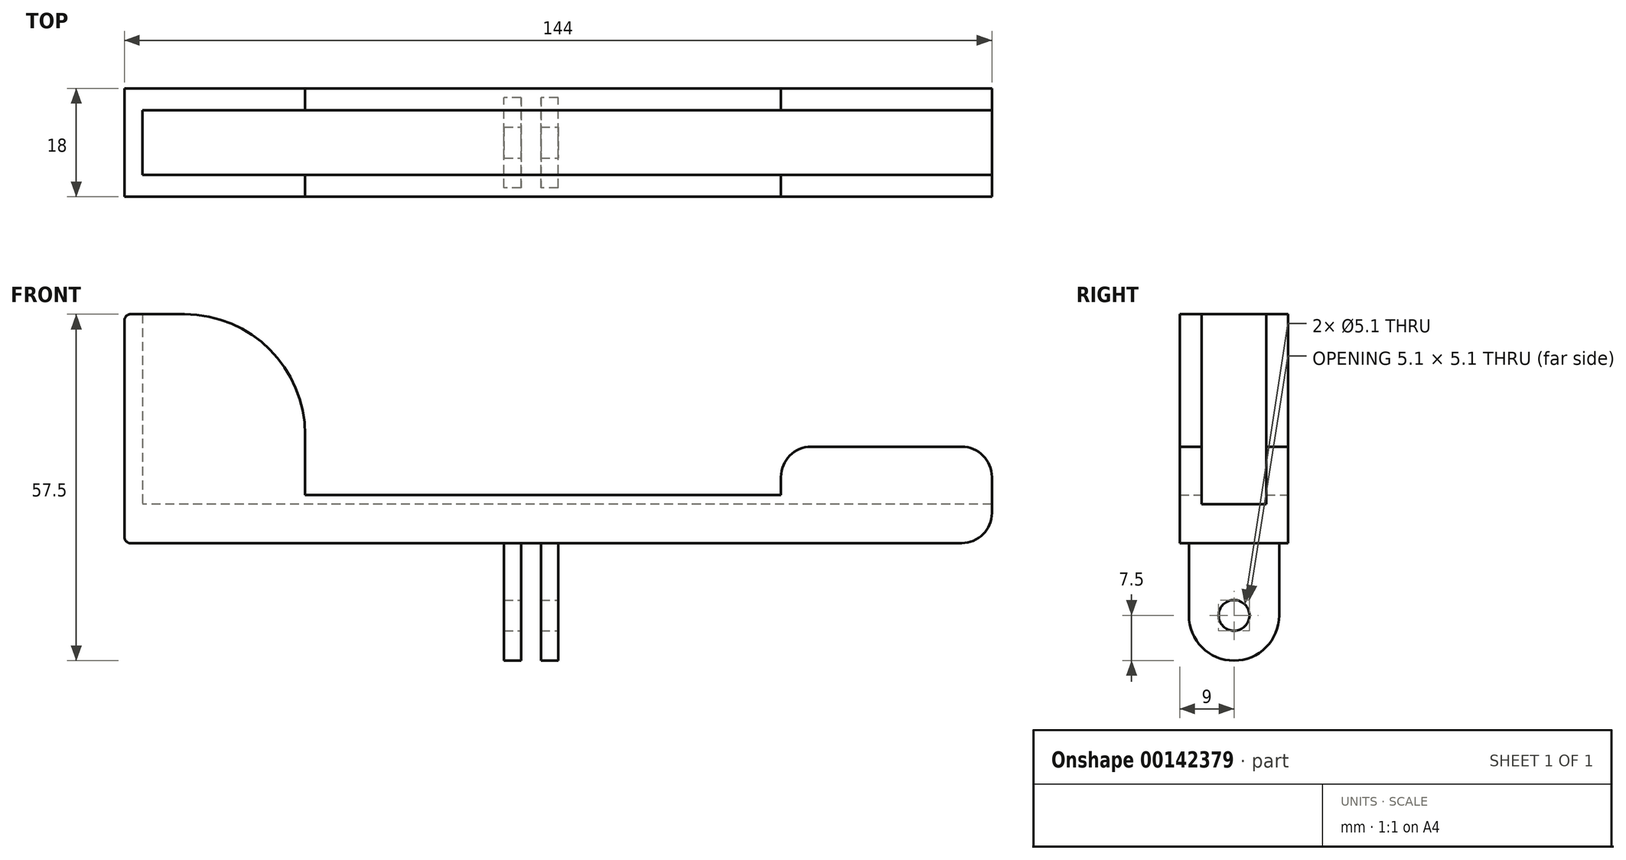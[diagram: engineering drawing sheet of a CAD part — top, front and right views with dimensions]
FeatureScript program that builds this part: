
annotation { "Feature Type Name" : "Feature", "Feature Type Description" : "" }
export const myFeature = defineFeature(function(context is Context, id is Id, definition is map)
    precondition{}
    {
        {
            var Q0;
            Q0=qCreatedBy(makeId("Right.planeOp"),FACE);
            var sketch = newSketch(context, id + "F0", { "sketchPlane" : qUnion([Q0])});
            skCircle(sketch, "E0", {"center": v(0, 0) * mm, "radius": 7.5 * mm});
            skSolve(sketch);
        }
        {
            var Q0;
            Q0=qCreatedBy(makeId("Right.planeOp"),FACE);
            var sketch = newSketch(context, id + "F1", { "sketchPlane" : qUnion([Q0])});
            skLineSegment(sketch, "E1.bottom", {"start": v(-7.5, 0) * mm, "end": v(7.5, 0) * mm});
            skLineSegment(sketch, "E1.top", {"start": v(-7.5, 12) * mm, "end": v(7.5, 12) * mm});
            skLineSegment(sketch, "E1.left", {"start": v(-7.5, 0) * mm, "end": v(-7.5, 12) * mm});
            skLineSegment(sketch, "E1.right", {"start": v(7.5, 0) * mm, "end": v(7.5, 12) * mm});
            skSolve(sketch);
        }
        {
            var Q0;
            Q0 = qSketchRegion(id + "F0", true);
            var Q1;
            Q1 = qSketchRegion(id + "F1", true);
            extrude(context, id + "F2", {"entities" : qUnion([Q0, Q1]), "flatOperationType" : FlatOperationType.REMOVE, "offsetDistance" : 25 * mm, "depth" : 9 * mm, "domain" : OperationDomain.MODEL, "symmetric" : true});
        }
        {
            var Q0;
            Q0=makeQuery(id+"F2.opExtrude","CAP_FACE",FACE,{"disambiguationData":[OSD([sQuery(id+"F1.wireOp",EDGE,"E1.bottom"),sQuery(id+"F1.wireOp",EDGE,"E1.top"),sQuery(id+"F1.wireOp",EDGE,"E1.left"),sQuery(id+"F1.wireOp",EDGE,"E1.right")])],"isStart":false});
            var sketch = newSketch(context, id + "F3", { "sketchPlane" : qUnion([Q0])});
            skLineSegment(sketch, "E2.bottom", {"start": v(-9, 12) * mm, "end": v(9, 12) * mm});
            skLineSegment(sketch, "E2.top", {"start": v(-9, 20) * mm, "end": v(9, 20) * mm});
            skLineSegment(sketch, "E2.left", {"start": v(-9, 12) * mm, "end": v(-9, 20) * mm});
            skLineSegment(sketch, "E2.right", {"start": v(9, 12) * mm, "end": v(9, 20) * mm});
            skSolve(sketch);
        }
        {
            var Q0;
            Q0 = qSketchRegion(id + "F3", true);
            extrude(context, id + "F4", {"entities" : qUnion([Q0]), "operationType" : NewBodyOperationType.ADD, "oppositeDirection" : true, "depth" : 144 * mm, "symmetric" : true});
        }
        {
            var Q0;
            Q0=qCreatedBy(makeId("Front.planeOp"),FACE);
            var sketch = newSketch(context, id + "F5", { "sketchPlane" : qUnion([Q0])});
            skLineSegment(sketch, "E3.bottom", {"start": v(-67.5, 20) * mm, "end": v(-37.5, 20) * mm});
            skLineSegment(sketch, "E3.top", {"start": v(-67.5, 50) * mm, "end": v(-37.5, 50) * mm});
            skLineSegment(sketch, "E3.left", {"start": v(-67.5, 20) * mm, "end": v(-67.5, 50) * mm});
            skLineSegment(sketch, "E3.right", {"start": v(-37.5, 20) * mm, "end": v(-37.5, 50) * mm});
            skSolve(sketch);
        }
        {
            var Q0;
            Q0=makeQuery(id+"F5.imprint","IMPRINT",FACE,{"disambiguationData":[TD([[makeQuery(id+"F5.imprint","IMPRINT",EDGE,{"derivedFrom":sQuery(id+"F5.wireOp",EDGE,"E3.bottom")}),1.0]])]});
            extrude(context, id + "F6", {"entities" : qUnion([Q0]), "oppositeDirection" : true, "depth" : 18 * mm, "offsetDistance" : 25 * mm, "symmetric" : true});
        }
        {
            var Q0;
            Q0=qCreatedBy(makeId("Front.planeOp"),FACE);
            var sketch = newSketch(context, id + "F7", { "sketchPlane" : qUnion([Q0])});
            skLineSegment(sketch, "E4.bottom", {"start": v(76.5, 20) * mm, "end": v(41.5, 20) * mm});
            skLineSegment(sketch, "E4.top", {"start": v(76.5, 28) * mm, "end": v(41.5, 28) * mm});
            skLineSegment(sketch, "E4.left", {"start": v(76.5, 20) * mm, "end": v(76.5, 28) * mm});
            skLineSegment(sketch, "E4.right", {"start": v(41.5, 20) * mm, "end": v(41.5, 28) * mm});
            skSolve(sketch);
        }
        {
            var Q0;
            Q0=makeQuery(id+"F7.imprint","IMPRINT",FACE,{"disambiguationData":[TD([[makeQuery(id+"F7.imprint","IMPRINT",EDGE,{"derivedFrom":sQuery(id+"F7.wireOp",EDGE,"E4.bottom")}),-1.0]])]});
            extrude(context, id + "F8", {"entities" : qUnion([Q0]), "depth" : 18 * mm, "offsetDistance" : 25 * mm, "symmetric" : true});
        }
        {
            var Q0;
            Q0=qCreatedBy(makeId("Front.planeOp"),FACE);
            var sketch = newSketch(context, id + "F9", { "sketchPlane" : qUnion([Q0])});
            skLineSegment(sketch, "E5.bottom", {"start": v(76.5, 53.5) * mm, "end": v(-64.5, 53.5) * mm});
            skLineSegment(sketch, "E5.top", {"start": v(76.5, 18.5) * mm, "end": v(-64.5, 18.5) * mm});
            skLineSegment(sketch, "E5.left", {"start": v(-64.5, 53.5) * mm, "end": v(-64.5, 18.5) * mm});
            skLineSegment(sketch, "E5.right", {"start": v(76.5, 53.5) * mm, "end": v(76.5, 18.5) * mm});
            skSolve(sketch);
        }
        {
            var Q0;
            Q0 = qSketchRegion(id + "F9", true);
            extrude(context, id + "F10", {"entities" : qUnion([Q0]), "depth" : 10.7 * mm, "flatOperationType" : FlatOperationType.REMOVE, "offsetDistance" : 25 * mm, "domain" : OperationDomain.MODEL, "symmetric" : true});
        }
        {
            var Q0;
            Q0=makeQuery(id+"F2.opExtrude","SWEPT_BODY",BODY,{"disambiguationData":[OSD([sQuery(id+"F0.wireOp",EDGE,"E0")])]});
            var Q1;
            Q1=makeQuery(id+"F2.opExtrude","SWEPT_BODY",BODY,{"disambiguationData":[OSD([sQuery(id+"F1.wireOp",EDGE,"E1.bottom"),sQuery(id+"F1.wireOp",EDGE,"E1.top"),sQuery(id+"F1.wireOp",EDGE,"E1.left"),sQuery(id+"F1.wireOp",EDGE,"E1.right")])]});
            var Q2;
            Q2=makeQuery(id+"F6.opExtrude","SWEPT_BODY",BODY,{"disambiguationData":[OSD([sQuery(id+"F5.wireOp",EDGE,"E3.bottom"),sQuery(id+"F5.wireOp",EDGE,"E3.top"),sQuery(id+"F5.wireOp",EDGE,"E3.left"),sQuery(id+"F5.wireOp",EDGE,"E3.right")])]});
            var Q3;
            Q3=makeQuery(id+"F8.opExtrude","SWEPT_BODY",BODY,{"disambiguationData":[OSD([sQuery(id+"F7.wireOp",EDGE,"E4.bottom"),sQuery(id+"F7.wireOp",EDGE,"E4.top"),sQuery(id+"F7.wireOp",EDGE,"E4.left"),sQuery(id+"F7.wireOp",EDGE,"E4.right")])]});
            booleanBodies(context, id + "F11", {"operationType" : BooleanOperationType.UNION, "tools" : qUnion([Q0, Q1, Q2, Q3])});
        }
        {
            var Q0;
            Q0=makeQuery(id+"F10.opExtrude","SWEPT_BODY",BODY,{"disambiguationData":[OSD([sQuery(id+"F9.wireOp",EDGE,"E5.bottom"),sQuery(id+"F9.wireOp",EDGE,"E5.top"),sQuery(id+"F9.wireOp",EDGE,"E5.left"),sQuery(id+"F9.wireOp",EDGE,"E5.right")])]});
            var Q1;
            Q1=makeQuery(id+"F2.opExtrude","SWEPT_BODY",BODY,{"disambiguationData":[OSD([sQuery(id+"F0.wireOp",EDGE,"E0")])]});
            booleanBodies(context, id + "F12", {"operationType" : BooleanOperationType.SUBTRACTION, "tools" : qUnion([Q0]), "targets" : qUnion([Q1])});
        }
        {
            var Q0;
            {var subQ0=sQuery(id+"F5.wireOp",EDGE,"E3.right");var subQ1=sQuery(id+"F5.wireOp",EDGE,"E3.bottom");var subQ2=sQuery(id+"F3.wireOp",EDGE,"E2.left");var subQ3=sQuery(id+"F3.wireOp",EDGE,"E2.top");Q0=makeQuery(id+"F12.opBoolean","SPLIT",EDGE,{"disambiguationData":[TD([makeQuery(id+"F2.opExtrude","SWEPT_FACE",FACE,{"disambiguationData":[OSD([sQuery(id+"F1.wireOp",EDGE,"E1.left")])]})])],"derivedFrom":makeQuery(id+"F6.opExtrude","SWEPT_EDGE",EDGE,{"disambiguationData":[OSD([subQ3,subQ2,subQ1,subQ0])]})});}
            var Q1;
            {var subQ0=sQuery(id+"F3.wireOp",EDGE,"E2.top");var subQ1=sQuery(id+"F5.wireOp",EDGE,"E3.right");var subQ2=sQuery(id+"F5.wireOp",EDGE,"E3.bottom");Q1=makeQuery(id+"F12.opBoolean","SPLIT",EDGE,{"disambiguationData":[TD([makeQuery(id+"F2.opExtrude","SWEPT_FACE",FACE,{"disambiguationData":[OSD([sQuery(id+"F1.wireOp",EDGE,"E1.right")])]})])],"derivedFrom":makeQuery(id+"F6.opExtrude","SWEPT_EDGE",EDGE,{"disambiguationData":[OSD([subQ0,sQuery(id+"F3.wireOp",EDGE,"E2.left"),subQ2,subQ1])]})});}
            var Q2;
            Q2=makeQuery(id+"F4.opExtrude","CAP_EDGE",EDGE,{"disambiguationData":[OSD([sQuery(id+"F3.wireOp",EDGE,"E2.top")])],"isStart":true});
            var Q3;
            Q3=makeQuery(id+"F2.opExtrude","CAP_EDGE",EDGE,{"disambiguationData":[OSD([sQuery(id+"F1.wireOp",EDGE,"E1.top")])],"isStart":true});
            var Q4;
            Q4=makeQuery(id+"F4.opExtrude","CAP_EDGE",EDGE,{"disambiguationData":[OSD([sQuery(id+"F3.wireOp",EDGE,"E2.bottom")])],"isStart":false});
            var Q5;
            Q5=makeQuery(id+"F6.opExtrude","SWEPT_EDGE",EDGE,{"disambiguationData":[OSD([sQuery(id+"F5.wireOp",EDGE,"E3.top"),sQuery(id+"F5.wireOp",EDGE,"E3.left")])]});
            var Q6;
            {var subQ0=sQuery(id+"F7.wireOp",EDGE,"E4.right");var subQ1=sQuery(id+"F7.wireOp",EDGE,"E4.bottom");Q6=makeQuery(id+"F12.opBoolean","SPLIT",EDGE,{"disambiguationData":[TD([makeQuery(id+"F2.opExtrude","SWEPT_FACE",FACE,{"disambiguationData":[OSD([sQuery(id+"F1.wireOp",EDGE,"E1.left")])]})])],"derivedFrom":makeQuery(id+"F8.opExtrude","SWEPT_EDGE",EDGE,{"disambiguationData":[OSD([subQ1,subQ0])]})});}
            var Q7;
            {var subQ0=sQuery(id+"F7.wireOp",EDGE,"E4.right");var subQ1=sQuery(id+"F7.wireOp",EDGE,"E4.bottom");Q7=makeQuery(id+"F12.opBoolean","SPLIT",EDGE,{"disambiguationData":[TD([makeQuery(id+"F2.opExtrude","SWEPT_FACE",FACE,{"disambiguationData":[OSD([sQuery(id+"F1.wireOp",EDGE,"E1.right")])]})])],"derivedFrom":makeQuery(id+"F8.opExtrude","SWEPT_EDGE",EDGE,{"disambiguationData":[OSD([subQ1,subQ0])]})});}
            var Q8;
            Q8=makeQuery(id+"F2.opExtrude","CAP_EDGE",EDGE,{"disambiguationData":[OSD([sQuery(id+"F1.wireOp",EDGE,"E1.top")])],"isStart":false});
            fillet(context, id + "F13", {"entities" : qUnion([Q0, Q1, Q2, Q3, Q4, Q5, Q6, Q7, Q8]), "radius" : 1 * mm, "tangentPropagation" : true, "allowEdgeOverflow" : false});
        }
        {
            var Q0;
            {var subQ0=sQuery(id+"F5.wireOp",EDGE,"E3.top");var subQ1=sQuery(id+"F5.wireOp",EDGE,"E3.right");Q0=makeQuery(id+"F12.opBoolean","SPLIT",EDGE,{"disambiguationData":[TD([makeQuery(id+"F2.opExtrude","SWEPT_FACE",FACE,{"disambiguationData":[OSD([sQuery(id+"F1.wireOp",EDGE,"E1.left")])]})])],"derivedFrom":makeQuery(id+"F6.opExtrude","SWEPT_EDGE",EDGE,{"disambiguationData":[OSD([subQ0,subQ1])]})});}
            var Q1;
            {var subQ0=sQuery(id+"F5.wireOp",EDGE,"E3.top");var subQ1=sQuery(id+"F5.wireOp",EDGE,"E3.right");Q1=makeQuery(id+"F12.opBoolean","SPLIT",EDGE,{"disambiguationData":[TD([makeQuery(id+"F2.opExtrude","SWEPT_FACE",FACE,{"disambiguationData":[OSD([sQuery(id+"F1.wireOp",EDGE,"E1.right")])]})])],"derivedFrom":makeQuery(id+"F6.opExtrude","SWEPT_EDGE",EDGE,{"disambiguationData":[OSD([subQ0,subQ1])]})});}
            var Q2;
            {var subQ0=sQuery(id+"F5.wireOp",EDGE,"E3.top");var subQ1=sQuery(id+"F5.wireOp",EDGE,"E3.right");Q2=makeQuery(id+"F12.opBoolean","SPLIT",EDGE,{"disambiguationData":[TD([makeQuery(id+"F4.opExtrude","SWEPT_FACE",FACE,{"disambiguationData":[OSD([sQuery(id+"F3.wireOp",EDGE,"E2.left")])]})])],"derivedFrom":makeQuery(id+"F6.opExtrude","SWEPT_EDGE",EDGE,{"disambiguationData":[OSD([subQ0,subQ1])]})});}
            var Q3;
            {var subQ0=sQuery(id+"F5.wireOp",EDGE,"E3.right");var subQ1=sQuery(id+"F5.wireOp",EDGE,"E3.top");Q3=makeQuery(id+"F12.opBoolean","SPLIT",EDGE,{"disambiguationData":[TD([makeQuery(id+"F4.opExtrude","SWEPT_FACE",FACE,{"disambiguationData":[OSD([sQuery(id+"F3.wireOp",EDGE,"E2.right")])]})])],"derivedFrom":makeQuery(id+"F6.opExtrude","SWEPT_EDGE",EDGE,{"disambiguationData":[OSD([subQ1,subQ0])]})});}
            fillet(context, id + "F14", {"entities" : qUnion([Q0, Q1, Q2, Q3]), "radius" : 20 * mm, "tangentPropagation" : true, "allowEdgeOverflow" : false});
        }
        {
            var Q0;
            {var subQ0=sQuery(id+"F5.wireOp",EDGE,"E3.right");var subQ1=sQuery(id+"F5.wireOp",EDGE,"E3.bottom");Q0=makeQuery(id+"F12.opBoolean","SPLIT",EDGE,{"disambiguationData":[TD([makeQuery(id+"F4.opExtrude","SWEPT_FACE",FACE,{"disambiguationData":[OSD([sQuery(id+"F3.wireOp",EDGE,"E2.left")])]})])],"derivedFrom":makeQuery(id+"F6.opExtrude","SWEPT_EDGE",EDGE,{"disambiguationData":[OSD([subQ1,subQ0])]})});}
            var Q1;
            {var subQ0=sQuery(id+"F7.wireOp",EDGE,"E4.top");var subQ1=sQuery(id+"F7.wireOp",EDGE,"E4.right");Q1=makeQuery(id+"F12.opBoolean","SPLIT",EDGE,{"disambiguationData":[TD([makeQuery(id+"F4.opExtrude","SWEPT_FACE",FACE,{"disambiguationData":[OSD([sQuery(id+"F3.wireOp",EDGE,"E2.left")])]})])],"derivedFrom":makeQuery(id+"F8.opExtrude","SWEPT_EDGE",EDGE,{"disambiguationData":[OSD([subQ0,subQ1])]})});}
            var Q2;
            {var subQ0=sQuery(id+"F7.wireOp",EDGE,"E4.right");var subQ1=sQuery(id+"F7.wireOp",EDGE,"E4.top");Q2=makeQuery(id+"F12.opBoolean","SPLIT",EDGE,{"disambiguationData":[TD([makeQuery(id+"F4.opExtrude","SWEPT_FACE",FACE,{"disambiguationData":[OSD([sQuery(id+"F3.wireOp",EDGE,"E2.right")])]})])],"derivedFrom":makeQuery(id+"F8.opExtrude","SWEPT_EDGE",EDGE,{"disambiguationData":[OSD([subQ1,subQ0])]})});}
            var Q3;
            {var subQ0=sQuery(id+"F7.wireOp",EDGE,"E4.left");var subQ1=sQuery(id+"F7.wireOp",EDGE,"E4.top");var subQ2=sQuery(id+"F3.wireOp",EDGE,"E2.right");Q3=makeQuery(id+"F12.opBoolean","SPLIT",EDGE,{"disambiguationData":[TD([makeQuery(id+"F4.opExtrude","SWEPT_FACE",FACE,{"disambiguationData":[OSD([subQ2])]})])],"derivedFrom":makeQuery(id+"F8.opExtrude","SWEPT_EDGE",EDGE,{"disambiguationData":[OSD([subQ1,subQ0])]})});}
            var Q4;
            {var subQ0=sQuery(id+"F7.wireOp",EDGE,"E4.left");var subQ1=sQuery(id+"F7.wireOp",EDGE,"E4.top");var subQ2=sQuery(id+"F3.wireOp",EDGE,"E2.left");Q4=makeQuery(id+"F12.opBoolean","SPLIT",EDGE,{"disambiguationData":[TD([makeQuery(id+"F4.opExtrude","SWEPT_FACE",FACE,{"disambiguationData":[OSD([subQ2])]})])],"derivedFrom":makeQuery(id+"F8.opExtrude","SWEPT_EDGE",EDGE,{"disambiguationData":[OSD([subQ1,subQ0])]})});}
            var Q5;
            Q5=makeQuery(id+"F4.opExtrude","CAP_EDGE",EDGE,{"disambiguationData":[OSD([sQuery(id+"F3.wireOp",EDGE,"E2.bottom")])],"isStart":true});
            var Q6;
            {var subQ0=sQuery(id+"F3.wireOp",EDGE,"E2.bottom");Q6=makeQuery(id+"F13.opFillet","BLEND_EDGE",EDGE,{"blendedFrom":[makeQuery(id+"F4.opExtrude","CAP_EDGE",EDGE,{"disambiguationData":[OSD([subQ0])],"isStart":false}),makeQuery(id+"F11.opBoolean","MERGE",FACE,{"derivedFrom":[makeQuery(id+"F4.opExtrude","CAP_FACE",FACE,{"disambiguationData":[OSD([subQ0,sQuery(id+"F3.wireOp",EDGE,"E2.top"),sQuery(id+"F3.wireOp",EDGE,"E2.left"),sQuery(id+"F3.wireOp",EDGE,"E2.right")])],"isStart":false}),makeQuery(id+"F6.opExtrude","SWEPT_FACE",FACE,{"disambiguationData":[OSD([sQuery(id+"F5.wireOp",EDGE,"E3.left")])]})]})],"blendedInto":[makeQuery(id+"F11.opBoolean","MERGE",FACE,{"derivedFrom":[makeQuery(id+"F4.opExtrude","CAP_FACE",FACE,{"disambiguationData":[OSD([subQ0,sQuery(id+"F3.wireOp",EDGE,"E2.top"),sQuery(id+"F3.wireOp",EDGE,"E2.left"),sQuery(id+"F3.wireOp",EDGE,"E2.right")])],"isStart":false}),makeQuery(id+"F6.opExtrude","SWEPT_FACE",FACE,{"disambiguationData":[OSD([sQuery(id+"F5.wireOp",EDGE,"E3.left")])]})]})]});}
            fillet(context, id + "F15", {"entities" : qUnion([Q0, Q1, Q2, Q3, Q4, Q5, Q6]), "radius" : 5 * mm, "tangentPropagation" : true, "allowEdgeOverflow" : false});
        }
        {
            var Q0;
            Q0=qCreatedBy(makeId("Front.planeOp"),FACE);
            var sketch = newSketch(context, id + "F16", { "sketchPlane" : qUnion([Q0])});
            skLineSegment(sketch, "E6.bottom", {"start": v(-1.65, -16) * mm, "end": v(1.65, -16) * mm});
            skLineSegment(sketch, "E6.top", {"start": v(-1.65, 12) * mm, "end": v(1.65, 12) * mm});
            skLineSegment(sketch, "E6.left", {"start": v(-1.65, -16) * mm, "end": v(-1.65, 12) * mm});
            skLineSegment(sketch, "E6.right", {"start": v(1.65, -16) * mm, "end": v(1.65, 12) * mm});
            skSolve(sketch);
        }
        {
            var Q0;
            Q0=makeQuery(id+"F16.imprint","IMPRINT",FACE,{"disambiguationData":[TD([[makeQuery(id+"F16.imprint","IMPRINT",EDGE,{"derivedFrom":sQuery(id+"F16.wireOp",EDGE,"E6.bottom")}),1.0]])]});
            extrude(context, id + "F17", {"entities" : qUnion([Q0]), "depth" : 25 * mm, "symmetric" : true});
        }
        {
            var Q0;
            Q0=makeQuery(id+"F17.opExtrude","SWEPT_BODY",BODY,{"disambiguationData":[OSD([sQuery(id+"F16.wireOp",EDGE,"E6.bottom"),sQuery(id+"F16.wireOp",EDGE,"E6.top"),sQuery(id+"F16.wireOp",EDGE,"E6.left"),sQuery(id+"F16.wireOp",EDGE,"E6.right")])]});
            var Q1;
            Q1=makeQuery(id+"F2.opExtrude","SWEPT_BODY",BODY,{"disambiguationData":[OSD([sQuery(id+"F0.wireOp",EDGE,"E0")])]});
            booleanBodies(context, id + "F18", {"operationType" : BooleanOperationType.SUBTRACTION, "tools" : qUnion([Q0]), "targets" : qUnion([Q1])});
        }
        {
            var Q0;
            Q0=makeQuery(id+"F11.opBoolean","MERGE",FACE,{"derivedFrom":[makeQuery(id+"F2.opExtrude","CAP_FACE",FACE,{"disambiguationData":[OSD([sQuery(id+"F0.wireOp",EDGE,"E0")])],"isStart":false}),makeQuery(id+"F4.boolean.opBoolean","MERGE",FACE,{"derivedFrom":[makeQuery(id+"F2.opExtrude","CAP_FACE",FACE,{"disambiguationData":[OSD([sQuery(id+"F1.wireOp",EDGE,"E1.bottom"),sQuery(id+"F1.wireOp",EDGE,"E1.top"),sQuery(id+"F1.wireOp",EDGE,"E1.left"),sQuery(id+"F1.wireOp",EDGE,"E1.right")])],"isStart":false}),makeQuery(id+"F4.opExtrude","CAP_FACE",FACE,{"disambiguationData":[OSD([sQuery(id+"F3.wireOp",EDGE,"E2.bottom"),sQuery(id+"F3.wireOp",EDGE,"E2.top"),sQuery(id+"F3.wireOp",EDGE,"E2.left"),sQuery(id+"F3.wireOp",EDGE,"E2.right")])],"isStart":true})]})]});
            var sketch = newSketch(context, id + "F19", { "sketchPlane" : qUnion([Q0])});
            skCircle(sketch, "E7", {"center": v(0, 0) * mm, "radius": 2.55 * mm});
            skSolve(sketch);
        }
        {
            var Q0;
            Q0 = qSketchRegion(id + "F19", true);
            extrude(context, id + "F20", {"entities" : qUnion([Q0]), "oppositeDirection" : true, "depth" : 25 * mm});
        }
        {
            var Q0;
            Q0=makeQuery(id+"F20.opExtrude","SWEPT_BODY",BODY,{"disambiguationData":[OSD([sQuery(id+"F19.wireOp",EDGE,"E7")])]});
            var Q1;
            Q1=makeQuery(id+"F2.opExtrude","SWEPT_BODY",BODY,{"disambiguationData":[OSD([sQuery(id+"F0.wireOp",EDGE,"E0")])]});
            booleanBodies(context, id + "F21", {"operationType" : BooleanOperationType.SUBTRACTION, "tools" : qUnion([Q0]), "targets" : qUnion([Q1])});
        }
    });
